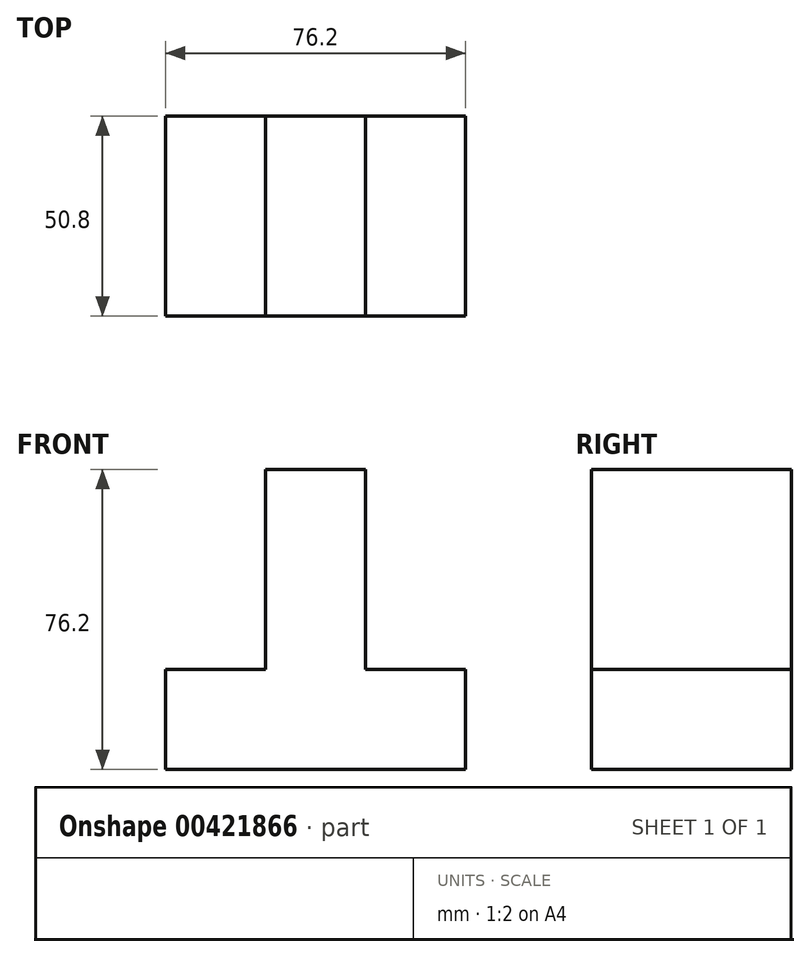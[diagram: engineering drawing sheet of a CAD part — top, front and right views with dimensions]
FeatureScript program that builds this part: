
annotation { "Feature Type Name" : "Feature", "Feature Type Description" : "" }
export const myFeature = defineFeature(function(context is Context, id is Id, definition is map)
    precondition{}
    {
        {
            var Q0;
            Q0=qCreatedBy(makeId("Front.planeOp"),FACE);
            var sketch = newSketch(context, id + "F0", { "sketchPlane" : qUnion([Q0])});
            skLineSegment(sketch, "E0", {"start": v(65.63, 0) * mm, "end": v(-10.57, 0) * mm});
            skLineSegment(sketch, "E1", {"start": v(-10.57, 0) * mm, "end": v(-10.57, 25.4) * mm});
            skLineSegment(sketch, "E2", {"start": v(-10.57, 25.4) * mm, "end": v(14.83, 25.4) * mm});
            skLineSegment(sketch, "E3", {"start": v(14.83, 25.4) * mm, "end": v(14.83, 76.2) * mm});
            skLineSegment(sketch, "E4", {"start": v(65.63, 0) * mm, "end": v(65.63, 25.4) * mm});
            skLineSegment(sketch, "E5", {"start": v(65.63, 25.4) * mm, "end": v(40.23, 25.4) * mm});
            skLineSegment(sketch, "E6", {"start": v(40.23, 25.4) * mm, "end": v(40.23, 76.2) * mm});
            skLineSegment(sketch, "E7", {"start": v(40.23, 76.2) * mm, "end": v(14.83, 76.2) * mm});
            skSolve(sketch);
        }
        {
            var Q0;
            Q0=makeQuery(id+"F0.imprint","IMPRINT",FACE,{"disambiguationData":[TD([[makeQuery(id+"F0.imprint","IMPRINT",EDGE,{"derivedFrom":sQuery(id+"F0.wireOp",EDGE,"E0")}),-1.0]])]});
            extrude(context, id + "F1", {"entities" : qUnion([Q0]), "depth" : 50.8 * mm});
        }
    });
